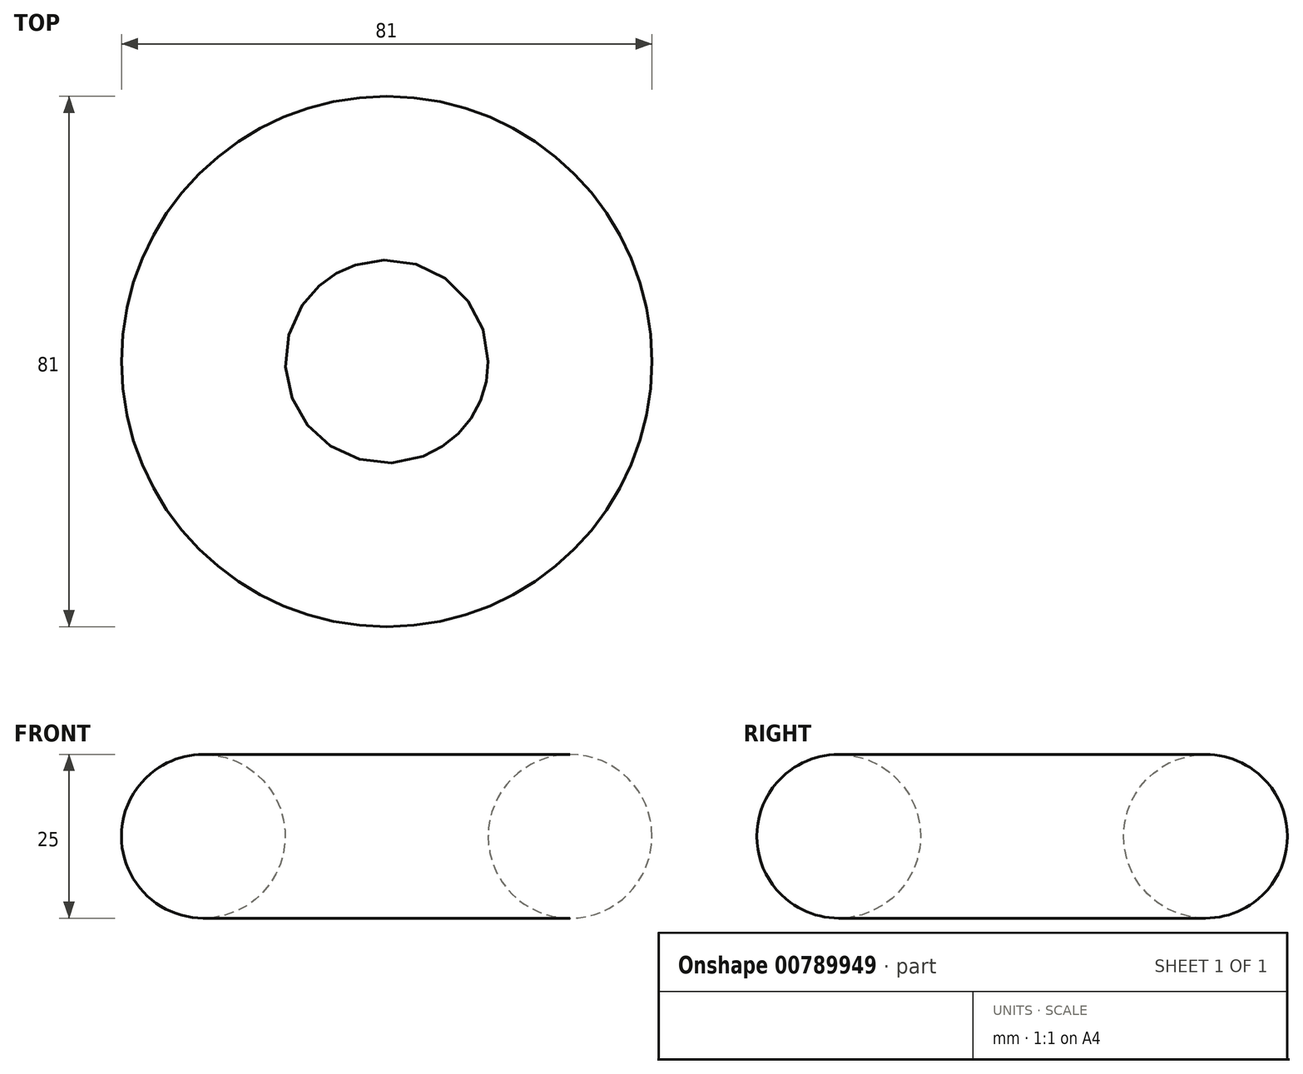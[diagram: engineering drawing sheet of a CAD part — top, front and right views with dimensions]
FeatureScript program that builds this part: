
annotation { "Feature Type Name" : "Feature", "Feature Type Description" : "" }
export const myFeature = defineFeature(function(context is Context, id is Id, definition is map)
    precondition{}
    {
        {
            var Q0;
            Q0=qCreatedBy(makeId("Right.planeOp"),FACE);
            var sketch = newSketch(context, id + "F0", { "sketchPlane" : qUnion([Q0])});
            skCircle(sketch, "E0", {"center": v(28, 0) * mm, "radius": 12.5 * mm});
            skLineSegment(sketch, "E1", {"start": v(0, -60.84) * mm, "end": v(0, 59.95) * mm, "construction": true});
            skSolve(sketch);
        }
        {
            var Q0;
            Q0=sQuery(id+"F0.wireOp",EDGE,"E0");
            var Q1;
            Q1=sQuery(id+"F0.wireOp",EDGE,"E1");
            revolve(context, id + "F1", {"bodyType" : ToolBodyType.SURFACE, "surfaceOperationType" : NewSurfaceOperationType.NEW, "surfaceEntities" : qUnion([Q0]), "axis" : qUnion([Q1]), "revolveType" : RevolveType.FULL});
        }
    });
